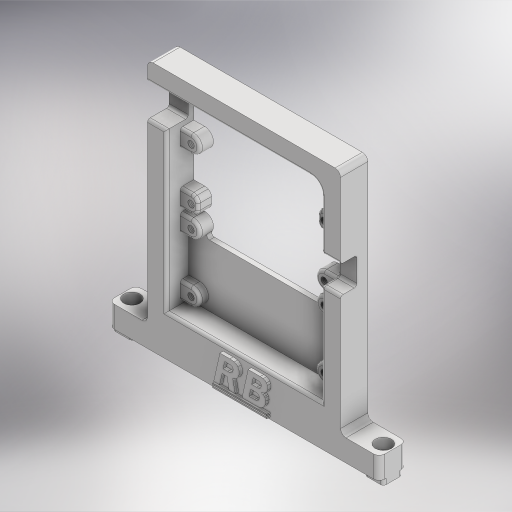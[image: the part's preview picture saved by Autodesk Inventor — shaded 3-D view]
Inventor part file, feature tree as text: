
AUTODESK INVENTOR PART (.ipt)
format: ipt  version: 2023 (Build 270158000, 158)  size: 1,038,336 bytes
history: native  units: mm
features: sketch x14, extrude x12, fillet x10, other x2, hole x2
ambient origin geometry x8: Origin, YZ Plane, XZ Plane, XY Plane, X Axis, Y Axis, Z Axis, Center Point
bodies: Body1 (feature_tree)
feature tree (40):
  other  "솔리드1"
  extrude  "돌출1"  Depth=55.0mm
  extrude  "돌출2"  Depth=68.0mm
  hole  "구멍1"  [1 undecoded]
  extrude  "돌출3"  Depth=3.0mm
  fillet  "모깎기1"  Radius=3.5mm
  fillet  "모깎기2"  Radius=3.0mm
  extrude  "돌출4"  Depth=3.5mm
  extrude  "돌출5"  Depth=3.0mm
  extrude  "돌출6"  Depth=3.0mm
  fillet  "모깎기3"  Radius=3.0mm
  fillet  "모깎기4"  Radius=33.0mm
  extrude  "돌출7"  Depth=33.0mm
  fillet  "모깎기5"  Radius=3.0mm
  fillet  "모깎기6"  Radius=3.0mm
  extrude  "돌출8"  Depth=8.0mm
  fillet  "모깎기7"  Radius=14.0mm
  fillet  "모깎기8"  Radius=3.0mm
  extrude  "돌출9"  Depth=3.0mm
  extrude  "돌출10"  Depth=25.0mm
  fillet  "모깎기9"  Radius=3.0mm
  fillet  "모깎기10"  Radius=3.0mm
  hole  "구멍2"  [1 undecoded]
  extrude  "돌출11"  Depth=3.0mm
  extrude  "돌출12"  Depth=3.0mm
  sketch  "스케치1"
  sketch  "스케치2"
  sketch  "스케치3"
  sketch  "스케치4"
  sketch  "스케치5"
  sketch  "스케치6"
  sketch  "스케치7"
  other  "이미지1"
  sketch  "스케치8"
  sketch  "스케치9"
  sketch  "스케치10"
  sketch  "스케치11"
  sketch  "스케치12"
  sketch  "스케치13"
  sketch  "스케치14"
note: 2 required parameter values undecoded (feature->parameter linkage not recoverable at this tier; creation-order binding heuristic only, values carry confidence <= 0.55)
